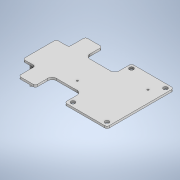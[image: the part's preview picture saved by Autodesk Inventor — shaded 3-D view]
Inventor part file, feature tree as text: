
AUTODESK INVENTOR PART (.ipt)
format: ipt  version: 2022 (Build 260153000, 153)  size: 232,960 bytes
history: native  units: mm
features: extrude x7, sketch x7, fillet x5
ambient origin geometry x8: Origin, YZ Plane, XZ Plane, XY Plane, X Axis, Y Axis, Z Axis, Center Point
bodies: Solid1 (feature_tree)
feature tree (19):
  extrude  "Extrusion1"  Depth=80.0mm
  extrude  "Extrusion2"  Depth=5.0mm
  fillet  "Fillet1"  Radius=5.0mm
  extrude  "Extrusion6"  Depth=5.0mm
  extrude  "Extrusion8"  Depth=5.0mm
  fillet  "Fillet3"  Radius=5.0mm
  fillet  "Fillet4"  Radius=5.0mm
  extrude  "Extrusion11"  Depth=5.0mm
  extrude  "Extrusion12"  Depth=5.0mm
  fillet  "Fillet5"  Radius=2.5mm
  fillet  "Fillet6"  Radius=2.5mm
  extrude  "Extrusion13"  Depth=40.0mm
  sketch  "Sketch1"  dims[d0=50.75mm d1=80.0mm]
  sketch  "Sketch2"  dims[d2=2.5mm d3=0.0mm d4=5.0mm d5=5.0mm]
  sketch  "Sketch6"  dims[d6=5.0mm d7=5.0mm]
  sketch  "Sketch8"  dims[d8=5.0mm d9=5.0mm d10=5.0mm d11=5.0mm]
  sketch  "Sketch11"  dims[d12=5.0mm d13=5.0mm]
  sketch  "Sketch12"  dims[d14=5.0mm d15=5.0mm d16=2.5mm d17=0.0mm d18=2.5mm]
  sketch  "Sketch13"  dims[d64=70.0mm d65=40.0mm d68=20.0mm d69=20.0mm d70=2.5mm d71=0.0mm d72=0.0mm d80=2.5mm d81=21.5mm d82=0.0mm d83=1.25mm d93=7.5mm d94=5.0mm d96=20.0mm d97=0.0mm d99=20.0mm d100=0.0mm d101=2.5mm d102=5.0mm d104=20.0mm d105=15.0mm d106=30.0mm d107=15.0mm d108=30.0mm d111=2.0mm d112=14.75mm d113=10.0mm d114=30.0mm d117=20.0mm d118=0.0mm d124=2.0mm d125=17.0mm d126=14.0mm]
